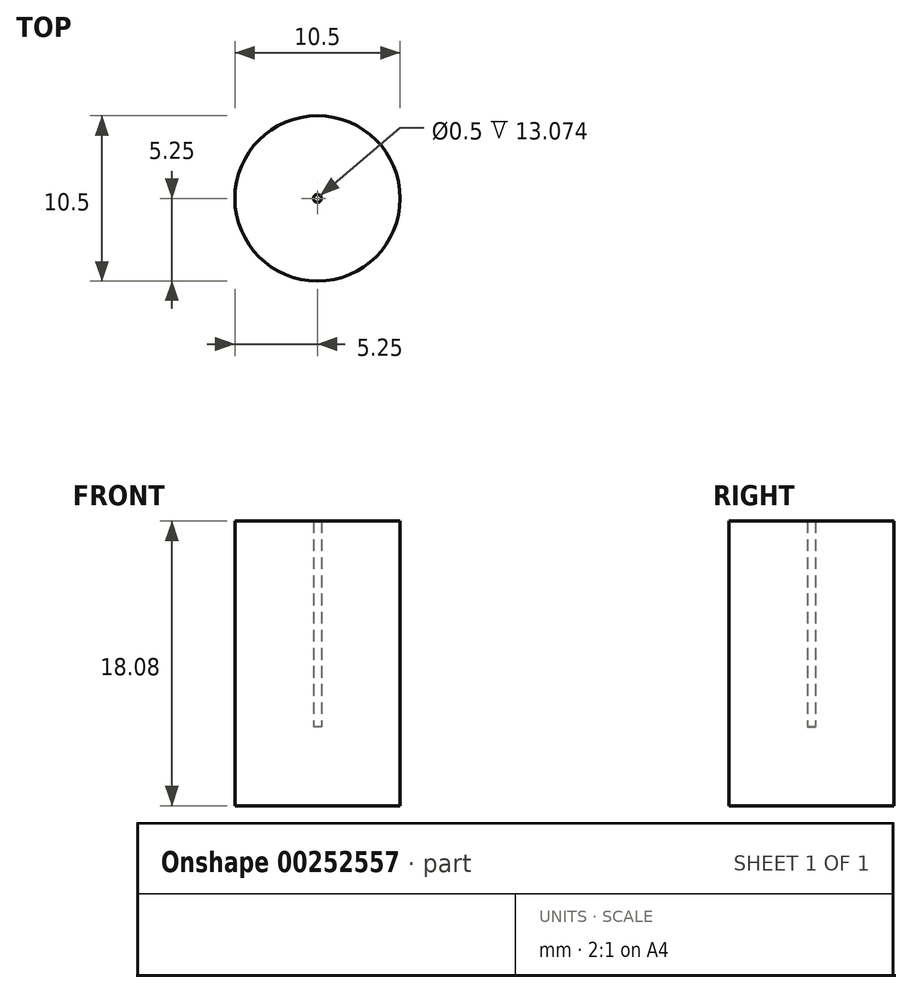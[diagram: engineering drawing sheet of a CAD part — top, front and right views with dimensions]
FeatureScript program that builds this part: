
annotation { "Feature Type Name" : "Feature", "Feature Type Description" : "" }
export const myFeature = defineFeature(function(context is Context, id is Id, definition is map)
    precondition{}
    {
        {
            var Q0;
            Q0=qCreatedBy(makeId("Front.planeOp"),FACE);
            var sketch = newSketch(context, id + "F0", { "sketchPlane" : qUnion([Q0])});
            skLineSegment(sketch, "E0.bottom", {"start": v(-5.25, -9.04) * mm, "end": v(5.25, -9.04) * mm});
            skLineSegment(sketch, "E0.top", {"start": v(-5.25, 9.04) * mm, "end": v(5.25, 9.04) * mm});
            skLineSegment(sketch, "E0.left", {"start": v(-5.25, -9.04) * mm, "end": v(-5.25, 9.04) * mm});
            skLineSegment(sketch, "E0.right", {"start": v(5.25, -9.04) * mm, "end": v(5.25, 9.04) * mm});
            skPoint(sketch, "E0.middle", {"position": v(0, 0) * mm});
            skLineSegment(sketch, "E1", {"start": v(0, 9.04) * mm, "end": v(0, -9.04) * mm});
            skSolve(sketch);
        }
        {
            var Q0;
            {var subQ0=sQuery(id+"F0.wireOp",EDGE,"E0.left");Q0=makeQuery(id+"F0.imprint","IMPRINT",FACE,{"disambiguationData":[TD([[makeQuery(id+"F0.imprint","IMPRINT",EDGE,{"derivedFrom":subQ0}),-1.0]])]});}
            var Q1;
            Q1=sQuery(id+"F0.wireOp",EDGE,"E1");
            revolve(context, id + "F1", {"entities" : qUnion([Q0]), "axis" : qUnion([Q1]), "revolveType" : RevolveType.FULL, "oppositeDirection" : true});
        }
        {
            var Q0;
            Q0=makeQuery(id+"F1.opRevolve","SWEPT_FACE",FACE,{"disambiguationData":[OSD([sQuery(id+"F0.wireOp",EDGE,"E0.top")])]});
            shell(context, id + "F2", {"entities" : qUnion([Q0]), "thickness" : 5 * mm});
        }
    });
